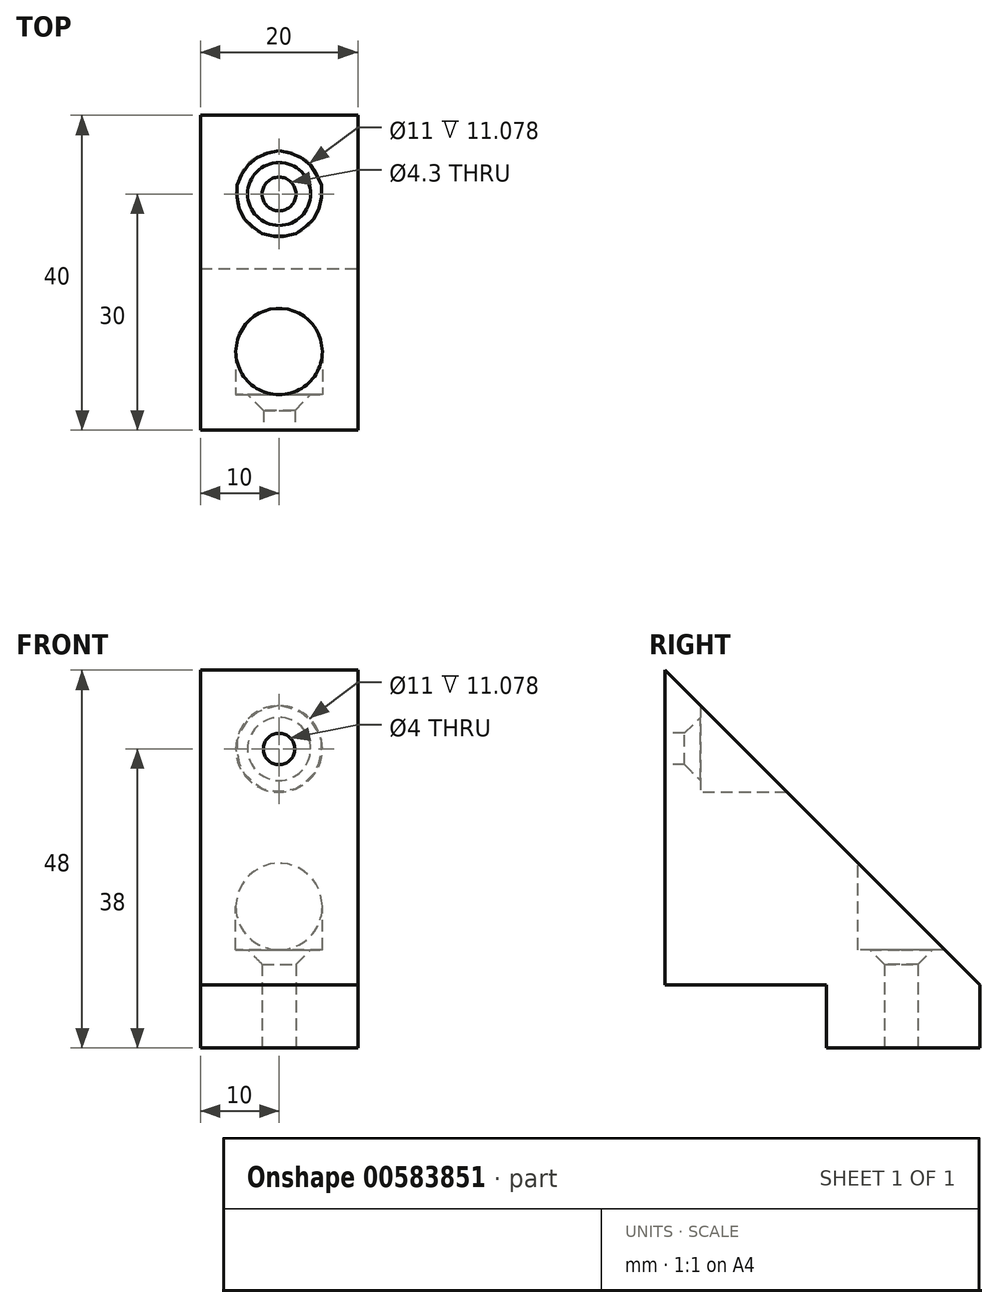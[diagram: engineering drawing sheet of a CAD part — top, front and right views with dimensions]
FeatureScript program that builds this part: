
annotation { "Feature Type Name" : "Feature", "Feature Type Description" : "" }
export const myFeature = defineFeature(function(context is Context, id is Id, definition is map)
    precondition{}
    {
        {
            var Q0;
            Q0=qCreatedBy(makeId("Top.planeOp"),FACE);
            var sketch = newSketch(context, id + "F0", { "sketchPlane" : qUnion([Q0])});
            skLineSegment(sketch, "E0.bottom", {"start": v(10, 20) * mm, "end": v(-10, 20) * mm});
            skLineSegment(sketch, "E0.top", {"start": v(10, -20) * mm, "end": v(-10, -20) * mm});
            skLineSegment(sketch, "E0.left", {"start": v(10, 20) * mm, "end": v(10, -20) * mm});
            skLineSegment(sketch, "E0.right", {"start": v(-10, 20) * mm, "end": v(-10, -20) * mm});
            skPoint(sketch, "E0.middle", {"position": v(0, 0) * mm});
            skLineSegment(sketch, "E1", {"start": v(0, 20) * mm, "end": v(0, -20) * mm, "construction": true});
            skLineSegment(sketch, "E2", {"start": v(-17.03, 10) * mm, "end": v(21.67, 10) * mm, "construction": true});
            skLineSegment(sketch, "E3", {"start": v(-18.95, -10) * mm, "end": v(21.99, -10) * mm, "construction": true});
            skPoint(sketch, "E4", {"position": v(0, 10) * mm});
            skPoint(sketch, "E5", {"position": v(0, -10) * mm});
            skSolve(sketch);
        }
        {
            var Q0;
            Q0=makeQuery(id+"F0.imprint","IMPRINT",FACE,{"disambiguationData":[TD([[makeQuery(id+"F0.imprint","IMPRINT",EDGE,{"derivedFrom":sQuery(id+"F0.wireOp",EDGE,"E0.bottom")}),1.0]])]});
            extrude(context, id + "F1", {"entities" : qUnion([Q0]), "depth" : 40 * mm, "offsetDistance" : 25 * mm});
        }
        {
            var Q0;
            Q0=qCreatedBy(makeId("Right.planeOp"),FACE);
            var sketch = newSketch(context, id + "F2", { "sketchPlane" : qUnion([Q0])});
            skLineSegment(sketch, "E6.0.0", {"start": v(-20, 0) * mm, "end": v(20, 0) * mm});
            skLineSegment(sketch, "E6.0.1", {"start": v(20, 0) * mm, "end": v(20, 40) * mm});
            skLineSegment(sketch, "E6.0.2", {"start": v(20, 40) * mm, "end": v(-20, 40) * mm});
            skLineSegment(sketch, "E6.0.3", {"start": v(-20, 40) * mm, "end": v(-20, 0) * mm});
            skLineSegment(sketch, "E7", {"start": v(-20, 40) * mm, "end": v(20, 0) * mm});
            skSolve(sketch);
        }
        {
            var Q0;
            Q0=makeQuery(id+"F2.imprint","IMPRINT",FACE,{"disambiguationData":[TD([[makeQuery(id+"F2.imprint","IMPRINT",EDGE,{"derivedFrom":sQuery(id+"F2.wireOp",EDGE,"E6.0.1")}),1.0]])]});
            extrude(context, id + "F3", {"entities" : qUnion([Q0]), "operationType" : NewBodyOperationType.REMOVE, "oppositeDirection" : true, "depth" : 25 * mm, "offsetDistance" : 25 * mm, "symmetric" : true});
        }
        {
            var Q0;
            Q0=makeQuery(id+"F0.imprint","IMPRINT",FACE,{"disambiguationData":[TD([[makeQuery(id+"F0.imprint","IMPRINT",EDGE,{"derivedFrom":sQuery(id+"F0.wireOp",EDGE,"E0.bottom")}),1.0]])]});
            cPlane(context, id + "F4", {"entities" : qUnion([Q0]), "cplaneType" : CPlaneType.OFFSET, "offset" : 10 * mm, "width" : 150 * mm, "height" : 150 * mm});
        }
        {
            var Q0;
            Q0=makeQuery(id+"F1.opExtrude","SWEPT_FACE",FACE,{"disambiguationData":[OSD([sQuery(id+"F0.wireOp",EDGE,"E0.top")])]});
            cPlane(context, id + "F5", {"entities" : qUnion([Q0]), "cplaneType" : CPlaneType.OFFSET, "offset" : 10 * mm, "oppositeDirection" : true, "width" : 150 * mm, "height" : 150 * mm});
        }
        {
            var Q0;
            Q0=qCreatedBy(id+"F4.planeOp",FACE);
            var sketch = newSketch(context, id + "F6", { "sketchPlane" : qUnion([Q0])});
            skPoint(sketch, "E8.0", {"position": v(0, 10) * mm});
            skPoint(sketch, "E9.0", {"position": v(0, -10) * mm});
            skCircle(sketch, "E10", {"center": v(0, 10) * mm, "radius": 5.5 * mm});
            skSolve(sketch);
        }
        {
            var Q0;
            Q0=makeQuery(id+"F6.imprint","IMPRINT",FACE,{"disambiguationData":[TD([[makeQuery(id+"F6.imprint","IMPRINT",EDGE,{"derivedFrom":sQuery(id+"F6.wireOp",EDGE,"E10")}),1.0]])]});
            extrude(context, id + "F7", {"entities" : qUnion([Q0]), "operationType" : NewBodyOperationType.REMOVE, "oppositeDirection" : true, "depth" : 11 * mm, "offsetDistance" : 25 * mm, "symmetric" : true});
        }
        {
            var Q0;
            Q0=makeQuery(id+"F7.boolean.opBoolean","COPY",FACE,{"derivedFrom":makeQuery(id+"F7.opExtrude","CAP_FACE",FACE,{"disambiguationData":[OSD([sQuery(id+"F6.wireOp",EDGE,"E10")])],"isStart":false})});
            var sketch = newSketch(context, id + "F8", { "sketchPlane" : qUnion([Q0])});
            skCircle(sketch, "E11.0.0", {"center": v(0, 10) * mm, "radius": 5.5 * mm, "construction": true});
            skSolve(sketch);
        }
        {
            var Q0;
            Q0=makeQuery(id+"F0.imprint","IMPRINT",FACE,{"disambiguationData":[TD([[makeQuery(id+"F0.imprint","IMPRINT",EDGE,{"derivedFrom":sQuery(id+"F0.wireOp",EDGE,"E0.bottom")}),1.0]])]});
            var sketch = newSketch(context, id + "F9", { "sketchPlane" : qUnion([Q0])});
            skLineSegment(sketch, "E12.0.0", {"start": v(10, -20) * mm, "end": v(10, 20) * mm});
            skLineSegment(sketch, "E12.0.1", {"start": v(10, 20) * mm, "end": v(-10, 20) * mm});
            skLineSegment(sketch, "E12.0.2", {"start": v(-10, 20) * mm, "end": v(-10, -20) * mm});
            skLineSegment(sketch, "E12.0.3", {"start": v(-10, -20) * mm, "end": v(10, -20) * mm});
            skLineSegment(sketch, "E13", {"start": v(-10, 0.5) * mm, "end": v(10, 0.5) * mm});
            skSolve(sketch);
        }
        {
            var Q0;
            {var subQ0=sQuery(id+"F9.wireOp",EDGE,"E12.0.1");Q0=makeQuery(id+"F9.imprint","IMPRINT",FACE,{"disambiguationData":[TD([[makeQuery(id+"F9.imprint","IMPRINT",EDGE,{"derivedFrom":subQ0}),1.0]])]});}
            extrude(context, id + "F10", {"entities" : qUnion([Q0]), "operationType" : NewBodyOperationType.ADD, "oppositeDirection" : true, "depth" : 8 * mm, "offsetDistance" : 25 * mm});
        }
        {
            var Q0;
            Q0=sQuery(id+"F8.wireOp",VERTEX,"E11.0.0.center");
            var Q1;
            Q1=makeQuery(id+"F1.opExtrude","SWEPT_BODY",BODY,{"disambiguationData":[OSD([sQuery(id+"F0.wireOp",EDGE,"E0.bottom"),sQuery(id+"F0.wireOp",EDGE,"E0.top"),sQuery(id+"F0.wireOp",EDGE,"E0.left"),sQuery(id+"F0.wireOp",EDGE,"E0.right")])]});
            hole(context, id + "F11", {"style" : HoleStyle.C_SINK, "endStyle" : HoleEndStyle.THROUGH, "holeDiameter" : 4.3 * mm, "cSinkDiameter" : 8 * mm, "cSinkAngle" : 90 * degree, "majorDiameter" : 5 * mm, "isTappedThrough" : true, "tappedDepth" : 12 * mm, "tapClearance" : 3, "locations" : qUnion([Q0]), "scope" : qUnion([Q1]), "startStyle" : HoleStartStyle.SKETCH});
        }
        {
            var Q0;
            Q0=qCreatedBy(id+"F5.planeOp",FACE);
            var sketch = newSketch(context, id + "F12", { "sketchPlane" : qUnion([Q0])});
            skLineSegment(sketch, "E14.0.0", {"start": v(10, 40) * mm, "end": v(10, 0) * mm});
            skLineSegment(sketch, "E14.0.1", {"start": v(10, 0) * mm, "end": v(-10, 0) * mm});
            skLineSegment(sketch, "E14.0.2", {"start": v(-10, 0) * mm, "end": v(-10, 40) * mm});
            skLineSegment(sketch, "E14.0.3", {"start": v(-10, 40) * mm, "end": v(10, 40) * mm});
            skLineSegment(sketch, "E15", {"start": v(-10, 30) * mm, "end": v(10, 30) * mm, "construction": true});
            skPoint(sketch, "E16", {"position": v(0, 30) * mm});
            skCircle(sketch, "E17", {"center": v(0, 30) * mm, "radius": 5.5 * mm});
            skSolve(sketch);
        }
        {
            var Q0;
            Q0=makeQuery(id+"F12.imprint","IMPRINT",FACE,{"disambiguationData":[TD([[makeQuery(id+"F12.imprint","IMPRINT",EDGE,{"derivedFrom":sQuery(id+"F12.wireOp",EDGE,"E17")}),1.0]])]});
            extrude(context, id + "F13", {"entities" : qUnion([Q0]), "operationType" : NewBodyOperationType.REMOVE, "oppositeDirection" : true, "depth" : 11 * mm, "offsetDistance" : 25 * mm, "symmetric" : true});
        }
        {
            var Q0;
            Q0=makeQuery(id+"F13.boolean.opBoolean","COPY",FACE,{"derivedFrom":makeQuery(id+"F13.opExtrude","CAP_FACE",FACE,{"disambiguationData":[OSD([sQuery(id+"F12.wireOp",EDGE,"E17")])],"isStart":true})});
            var sketch = newSketch(context, id + "F14", { "sketchPlane" : qUnion([Q0])});
            skPoint(sketch, "E18.0", {"position": v(0, 30) * mm});
            skSolve(sketch);
        }
        {
            var Q0;
            Q0=sQuery(id+"F14.wireOp",VERTEX,"E18.0");
            var Q1;
            Q1=makeQuery(id+"F1.opExtrude","SWEPT_BODY",BODY,{"disambiguationData":[OSD([sQuery(id+"F0.wireOp",EDGE,"E0.bottom"),sQuery(id+"F0.wireOp",EDGE,"E0.top"),sQuery(id+"F0.wireOp",EDGE,"E0.left"),sQuery(id+"F0.wireOp",EDGE,"E0.right")])]});
            hole(context, id + "F15", {"style" : HoleStyle.C_SINK, "endStyle" : HoleEndStyle.THROUGH, "holeDiameter" : 4 * mm, "cSinkDiameter" : 8 * mm, "cSinkAngle" : 90 * degree, "majorDiameter" : 5 * mm, "isTappedThrough" : true, "tappedDepth" : 12 * mm, "tapClearance" : 3, "locations" : qUnion([Q0]), "scope" : qUnion([Q1]), "startStyle" : HoleStartStyle.SKETCH});
        }
    });
